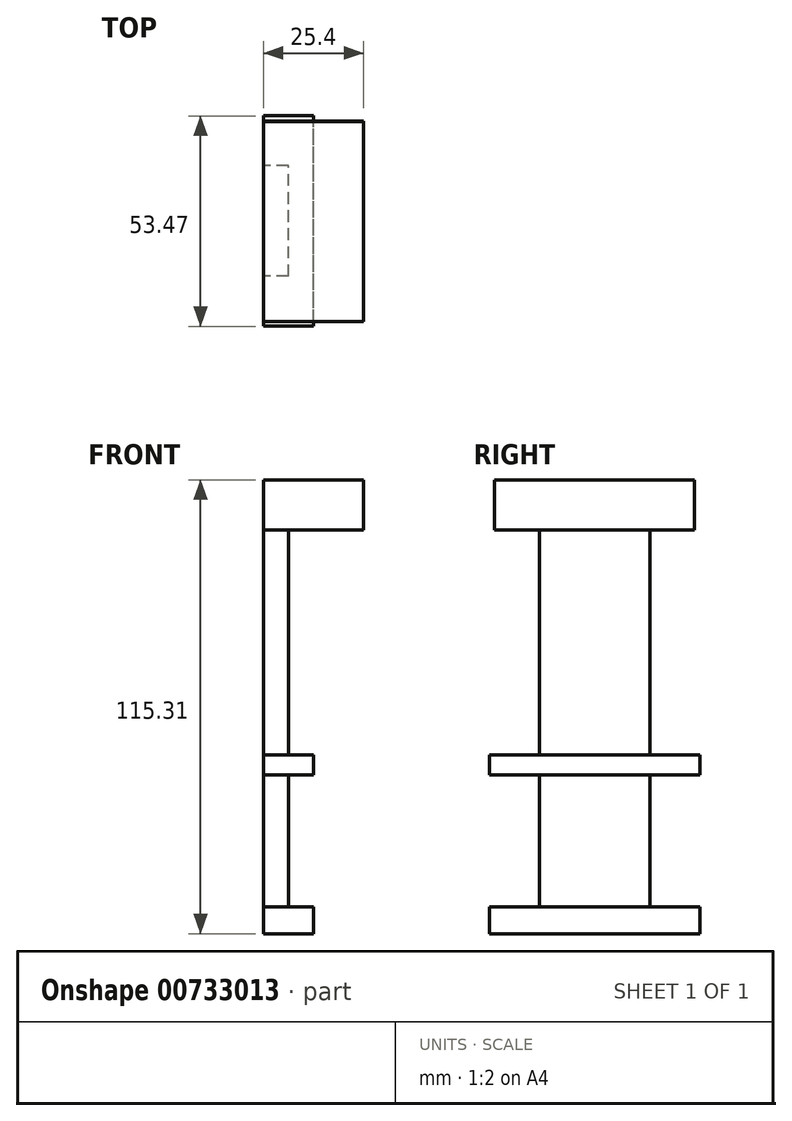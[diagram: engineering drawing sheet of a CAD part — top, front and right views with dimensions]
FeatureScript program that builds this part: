
annotation { "Feature Type Name" : "Feature", "Feature Type Description" : "" }
export const myFeature = defineFeature(function(context is Context, id is Id, definition is map)
    precondition{}
    {
        {
            var Q0;
            Q0=qCreatedBy(makeId("Right.planeOp"),FACE);
            var sketch = newSketch(context, id + "F0", { "sketchPlane" : qUnion([Q0])});
            skLineSegment(sketch, "E0", {"start": v(-18.24, 61.3) * mm, "end": v(-29.6, 61.3) * mm});
            skLineSegment(sketch, "E1", {"start": v(-29.7, 74) * mm, "end": v(21.1, 74) * mm});
            skLineSegment(sketch, "E2", {"start": v(-29.7, 74) * mm, "end": v(-29.6, 61.3) * mm});
            skLineSegment(sketch, "E3", {"start": v(-18.24, 61.3) * mm, "end": v(21.2, 61.3) * mm});
            skLineSegment(sketch, "E4", {"start": v(21.1, 74) * mm, "end": v(21.2, 61.3) * mm});
            skLineSegment(sketch, "E5", {"start": v(9.83, 61.3) * mm, "end": v(21.2, 61.3) * mm});
            skLineSegment(sketch, "E6", {"start": v(-18.24, 61.3) * mm, "end": v(-18.24, 4.15) * mm});
            skLineSegment(sketch, "E7", {"start": v(9.83, 61.3) * mm, "end": v(9.83, 4.15) * mm});
            skLineSegment(sketch, "E8", {"start": v(-18.24, 4.15) * mm, "end": v(9.83, 4.15) * mm});
            skLineSegment(sketch, "E9", {"start": v(-18.24, 4.15) * mm, "end": v(-30.94, 4.15) * mm});
            skLineSegment(sketch, "E10", {"start": v(9.83, 4.15) * mm, "end": v(22.53, 4.15) * mm});
            skLineSegment(sketch, "E11", {"start": v(-30.94, 4.15) * mm, "end": v(-30.94, -0.95) * mm});
            skLineSegment(sketch, "E12", {"start": v(22.53, 4.15) * mm, "end": v(22.53, -0.95) * mm});
            skLineSegment(sketch, "E13", {"start": v(-30.94, -0.95) * mm, "end": v(22.53, -0.95) * mm});
            skLineSegment(sketch, "E14", {"start": v(-18.24, -0.95) * mm, "end": v(-18.24, -34.48) * mm});
            skLineSegment(sketch, "E15", {"start": v(9.83, -0.95) * mm, "end": v(9.83, -34.48) * mm});
            skLineSegment(sketch, "E16", {"start": v(-18.24, -34.48) * mm, "end": v(9.83, -34.48) * mm});
            skLineSegment(sketch, "E17", {"start": v(-18.24, -34.48) * mm, "end": v(-30.94, -34.48) * mm});
            skLineSegment(sketch, "E18", {"start": v(-30.94, -34.48) * mm, "end": v(-30.94, -41.3) * mm});
            skLineSegment(sketch, "E19", {"start": v(9.83, -34.48) * mm, "end": v(22.53, -34.48) * mm});
            skLineSegment(sketch, "E20", {"start": v(22.53, -34.48) * mm, "end": v(22.53, -41.3) * mm});
            skLineSegment(sketch, "E21", {"start": v(-30.94, -41.3) * mm, "end": v(22.53, -41.3) * mm});
            skSolve(sketch);
        }
        {
            var Q0;
            Q0=makeQuery(id+"F0.imprint","IMPRINT",FACE,{"disambiguationData":[TD([[makeQuery(id+"F0.imprint","IMPRINT",EDGE,{"derivedFrom":sQuery(id+"F0.wireOp",EDGE,"E3")}),-1.0]])]});
            var Q1;
            {var subQ0=sQuery(id+"F0.wireOp",EDGE,"E14");Q1=makeQuery(id+"F0.imprint","IMPRINT",FACE,{"disambiguationData":[TD([[makeQuery(id+"F0.imprint","IMPRINT",EDGE,{"derivedFrom":subQ0}),1.0]])]});}
            extrude(context, id + "F1", {"entities" : qUnion([Q0, Q1]), "depth" : 6.35 * mm, "offsetDistance" : 25.4 * mm});
        }
        {
            var Q0;
            Q0=makeQuery(id+"F0.imprint","IMPRINT",FACE,{"disambiguationData":[TD([[makeQuery(id+"F0.imprint","IMPRINT",EDGE,{"derivedFrom":sQuery(id+"F0.wireOp",EDGE,"E0")}),-1.0]])]});
            extrude(context, id + "F2", {"entities" : qUnion([Q0]), "operationType" : NewBodyOperationType.ADD, "depth" : 25.4 * mm, "offsetDistance" : 25.4 * mm});
        }
        {
            var Q0;
            Q0=makeQuery(id+"F0.imprint","IMPRINT",FACE,{"disambiguationData":[TD([[makeQuery(id+"F0.imprint","IMPRINT",EDGE,{"derivedFrom":sQuery(id+"F0.wireOp",EDGE,"E8")}),-1.0]])]});
            var Q1;
            Q1=makeQuery(id+"F0.imprint","IMPRINT",FACE,{"disambiguationData":[TD([[makeQuery(id+"F0.imprint","IMPRINT",EDGE,{"derivedFrom":sQuery(id+"F0.wireOp",EDGE,"E16")}),-1.0]])]});
            extrude(context, id + "F3", {"entities" : qUnion([Q0, Q1]), "depth" : 12.7 * mm, "offsetDistance" : 25.4 * mm});
        }
    });
